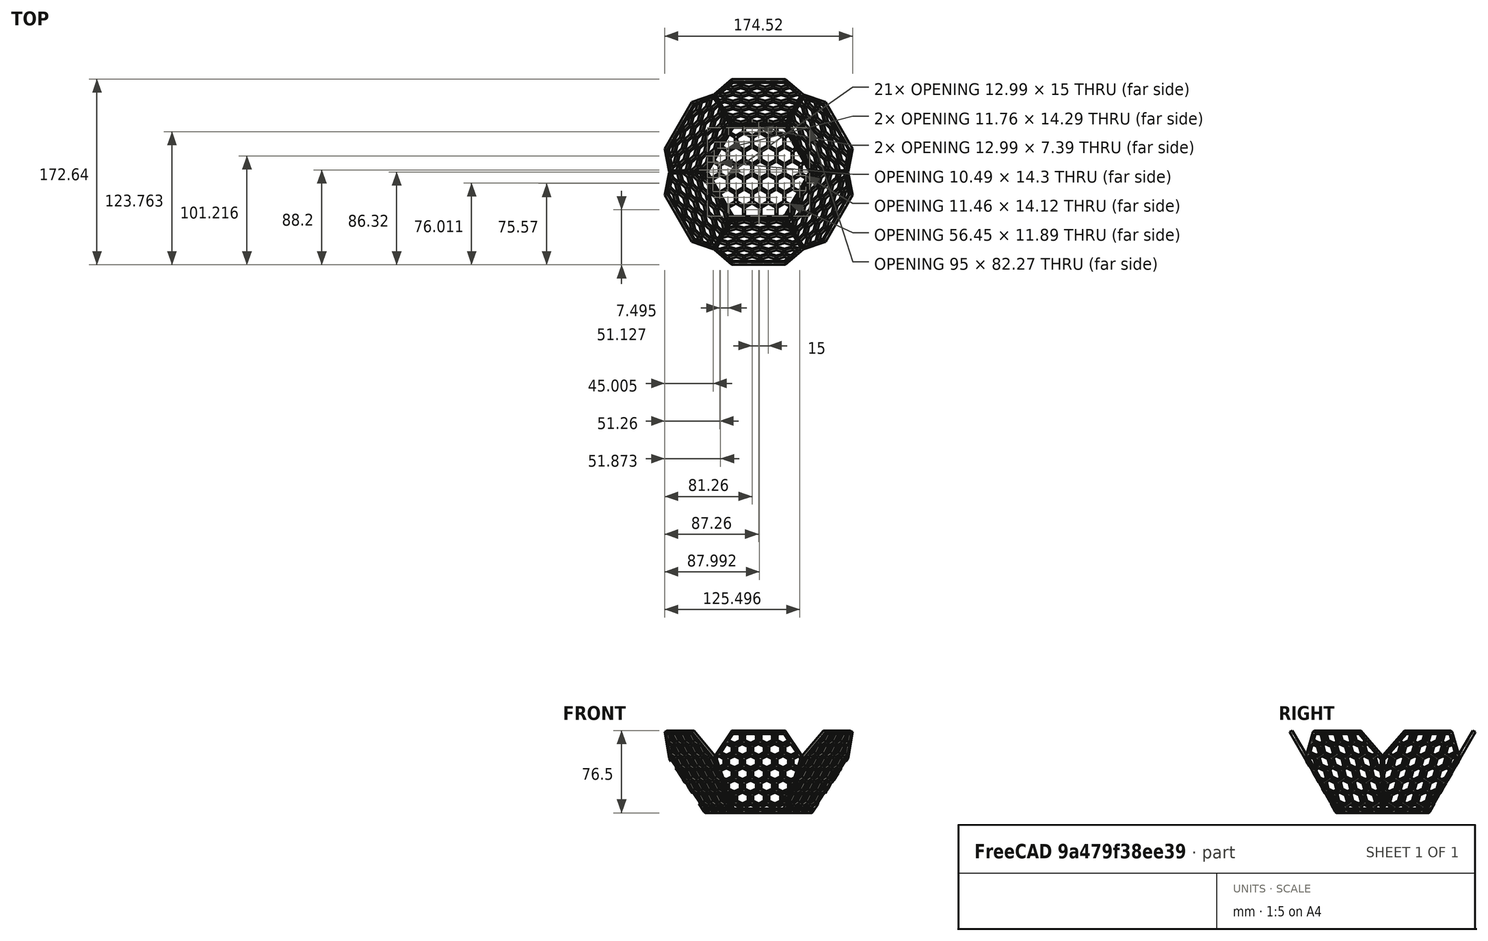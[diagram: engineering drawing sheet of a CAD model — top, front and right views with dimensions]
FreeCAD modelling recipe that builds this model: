
FCSTD DOCUMENT  (FreeCAD 0.20R29410 (Git))
Label: hexagon.v3
License: All rights reserved
LicenseURL: http://en.wikipedia.org/wiki/All_rights_reserved
objects: PartDesign::Body×8, Sketcher::SketchObject×6, Part::Cut×5, PartDesign::FeatureBase×4, Part::FeaturePython×3, Part::Extrusion×3, PartDesign::Pad×3, Part::Compound×2, Part::MultiFuse×2, Part::Mirroring×2, Part::Fuse×2, Spreadsheet::Sheet×1, Mesh::Feature×1
note: 42 computed .brp shape members not serialized (recipe doc carries the construction recipe); baked Part::Feature solids carry a one-line shape summary decoded from their .brp

FEATURE [Sketcher::SketchObject] Sketch  label="sHonycomb"
  FullyConstrained = true
  MapMode = 5
  Support = -> [XY_Plane]
  expr: .Constraints.HexR = <<Data>>.sHex_r
  expr: .Constraints.sHexD = <<Data>>.sHex_d
  sketch-geometry (18):
    g0: LineSegment StartX=0 StartY=11.25 StartZ=0 EndX=-6.49519 EndY=7.5 EndZ=0
    g1: LineSegment StartX=-6.49519 StartY=7.5 StartZ=0 EndX=-6.49519 EndY=9e-16 EndZ=0
    g2: LineSegment StartX=-6.49519 StartY=1e-15 StartZ=0 EndX=-9e-16 EndY=-3.75 EndZ=0
    g3: LineSegment StartX=-9e-16 StartY=-3.75 StartZ=0 EndX=6.49519 EndY=0 EndZ=0
    g4: LineSegment StartX=6.49519 StartY=0 StartZ=0 EndX=6.49519 EndY=7.5 EndZ=0
    g5: LineSegment StartX=6.49519 StartY=7.5 StartZ=0 EndX=0 EndY=11.25 EndZ=0
    g6: Circle CenterX=-1.1e-15 CenterY=3.75 CenterZ=0 NormalX=0 NormalY=0 NormalZ=1 AngleXU=0 Radius=7.5
    g7: LineSegment StartX=13.9904 StartY=-5.48205 StartZ=0 EndX=7.49519 EndY=-1.73205 EndZ=0
    g8: LineSegment StartX=7.49519 StartY=-1.73205 StartZ=0 EndX=1 EndY=-5.48205 EndZ=0
    g9: LineSegment StartX=1 StartY=-5.48205 StartZ=0 EndX=1 EndY=-12.9821 EndZ=0
    g10: LineSegment StartX=1 StartY=-12.9821 StartZ=0 EndX=7.49519 EndY=-16.7321 EndZ=0
    g11: LineSegment StartX=7.49519 StartY=-16.7321 StartZ=0 EndX=13.9904 EndY=-12.9821 EndZ=0
    g12: LineSegment StartX=13.9904 StartY=-12.9821 StartZ=0 EndX=13.9904 EndY=-5.48205 EndZ=0
    g13: Circle CenterX=7.49519 CenterY=-9.23205 CenterZ=0 NormalX=0 NormalY=0 NormalZ=1 AngleXU=0 Radius=7.5
    g14: LineSegment StartX=6.49519 StartY=0 StartZ=0 EndX=7.49519 EndY=-1.73205 EndZ=0
    g15: LineSegment StartX=7.49519 StartY=-1.73205 StartZ=0 EndX=8.49519 EndY=0 EndZ=0
    g16: LineSegment StartX=8.49519 StartY=0 StartZ=0 EndX=6.49519 EndY=0 EndZ=0
    g17: LineSegment StartX=6.49519 StartY=0 StartZ=0 EndX=-6.49519 EndY=1e-15 EndZ=0
  constraints (43):
    c: Coincident(g0,g1)
    c: Coincident(g1,g2)
    c: Coincident(g2,g3)
    c: Coincident(g3,g4)
    c: Coincident(g4,g5)
    c: Coincident(g5,g0)
    c: Equal(g0, g1-g5) x5
    c: PointOnObject(g0,g6)
    c: PointOnObject(g1,g6)
    c: PointOnObject(g2,g6)
    c: PointOnObject(g3,g6)
    c: PointOnObject(g4,g6)
    c: PointOnObject(g5,g6)
    c: Coincident(g7,g8)
    c: Coincident(g8,g9)
    c: Coincident(g9,g10)
    c: Coincident(g10,g11)
    c: Coincident(g11,g12)
    c: Coincident(g12,g7)
    c: Equal(g7, g8-g12) x5
    c: PointOnObject(g7,g13)
    c: PointOnObject(g8,g13)
    c: PointOnObject(g9,g13)
    c: PointOnObject(g10,g13)
    c: PointOnObject(g11,g13)
    c: PointOnObject(g12,g13)
    c: Equal(g6,g13)
    c: PointOnObject(g0,g-2)
    c: Vertical(g12)
    c: Radius(g6) = 7.5  'HexR'
    c: Vertical(g4)
    c: Coincident(g3,g14)
    c: Coincident(g14,g7)
    c: Coincident(g14,g15)
    c: PointOnObject(g15,g-1)
    c: Coincident(g15,g16)
    c: Coincident(g16,g14)
    c: Horizontal(g16)
    c: Equal(g15,g14)
    c: Equal(g14,g16)
    c: Distance(g16) = 2  'sHexD'
    c: Coincident(g17,g3)
    c: Coincident(g17,g1)
FEATURE [PartDesign::Body] Body  label="bHonycomSketch"
  Group = -> [Sketch]
  Origin = -> Origin
FEATURE [Part::FeaturePython] Array  label="ArrayofHonyComb"  # Draft array (typed FeaturePython)
  AlwaysSyncPlacement = false
  Angle = 360
  ArrayType = 0
  Axis = (0,0,1)
  Base = -> Sketch
  Center = (0,0,0)
  Count = 45
  ExpandArray = false
  Fuse = false
  IntervalAxis = (0,0,0)
  IntervalX = (15,0,0)
  IntervalY = (0,26,0)
  IntervalZ = (0,0,100)
  NumberCircles = 3
  NumberPolar = 5
  NumberX = 9
  NumberY = 5
  NumberZ = 1
  Placement = pos=(-81,-44,0) rot=(0,0,1;0rad)
  PlacementList = 45 placements: [(0,0,0),(0,26,0),(0,52,0),(0,78,0),(0,104,0),(15,0,0),(15,26,0),(15,52,0),(15,78,0),(15,104,0),(30,0,0),(30,26,0),(30,52,0),(30,78,0),(30,104,0),(45,0,0),(45,26,0),(45,52,0),(45,78,0),(45,104,0),(60,0,0),(60,26,0),(60,52,0),(60,78,0),(60,104,0),(75,0,0),(75,26,0),(75,52,0),(75,78,0),(75,104,0),(90,0,0),(90,26,0),(90,52,0),(90,78,0),(90,104,0),(105,0,0),(105,26,0),(105,52,0),(105,78,0),(105,104,0),+5 more]
  RadialDistance = 50
  ScaleList = (45) [(1,1,1),(1,1,1),(1,1,1),(1,1,1),(1,1,1),(1,1,1),(1,1,1),(1,1,1),(1,1,1),(1,1,1),(1,1,1),(1,1,1),(1,1,1),(1,1,1),(1,1,1),(1,1,1),(1,1,1),(1,1,1),+27 more]
  Symmetry = 1
  TangentialDistance = 25
FEATURE [Part::Extrusion] Extrude  label="HonyCombPart"
  Base = -> Array
  Dir = (0,0,1)
  DirMode = 2
  FaceMakerClass = Part::FaceMakerBullseye
  LengthFwd = 4
  LengthRev = 0
  Solid = true
  Symmetric = false
FEATURE [Sketcher::SketchObject] Sketch001  label="sHex"
  FullyConstrained = true
  MapMode = 5
  Support = -> [XY_Plane001]
  expr: Constraints[18] = <<Data>>.sFace_d - <<Data>>.sRing_w
  expr: Constraints[39] = <<Data>>.sFace_d
  sketch-geometry (14):
    g0: LineSegment StartX=23.75 StartY=41.1362 StartZ=0 EndX=-23.75 EndY=41.1362 EndZ=0
    g1: LineSegment StartX=-23.75 StartY=41.1362 StartZ=0 EndX=-47.5 EndY=8.53e-14 EndZ=0
    g2: LineSegment StartX=-47.5 StartY=8.71e-14 StartZ=0 EndX=-23.75 EndY=-41.1362 EndZ=0
    g3: LineSegment StartX=-23.75 StartY=-41.1362 StartZ=0 EndX=23.75 EndY=-41.1362 EndZ=0
    g4: LineSegment StartX=23.75 StartY=-41.1362 StartZ=0 EndX=47.5 EndY=7.82e-14 EndZ=0
    g5: LineSegment StartX=47.5 StartY=7.83e-14 StartZ=0 EndX=23.75 EndY=41.1362 EndZ=0
    g6: Circle CenterX=0 CenterY=0 CenterZ=0 NormalX=0 NormalY=0 NormalZ=1 AngleXU=0 Radius=47.5
    g7: LineSegment StartX=-25 StartY=43.3013 StartZ=0 EndX=-50 EndY=0 EndZ=0
    g8: LineSegment StartX=-50 StartY=-8e-16 StartZ=0 EndX=-25 EndY=-43.3013 EndZ=0
    g9: LineSegment StartX=-25 StartY=-43.3013 StartZ=0 EndX=25 EndY=-43.3013 EndZ=0
    g10: LineSegment StartX=25 StartY=-43.3013 StartZ=0 EndX=50 EndY=7.1e-15 EndZ=0
    g11: LineSegment StartX=50 StartY=3.8e-15 StartZ=0 EndX=25 EndY=43.3013 EndZ=0
    g12: LineSegment StartX=25 StartY=43.3013 StartZ=0 EndX=-25 EndY=43.3013 EndZ=0
    g13: Circle CenterX=0 CenterY=0 CenterZ=0 NormalX=0 NormalY=0 NormalZ=1 AngleXU=0 Radius=50
  constraints (32):
    c: Coincident(g0,g1)
    c: Coincident(g1,g2)
    c: Coincident(g2,g3)
    c: Coincident(g3,g4)
    c: Coincident(g4,g5)
    c: Coincident(g5,g0)
    c: Equal(g0, g1-g5) x5
    c: PointOnObject(g0,g6)
    c: PointOnObject(g1,g6)
    c: PointOnObject(g2,g6)
    c: PointOnObject(g3,g6)
    c: PointOnObject(g4,g6)
    c: PointOnObject(g5,g6)
    c: Coincident(g6,g-1)
    c: Diameter(g6) = 95
    c: Horizontal(g0)
    c: Coincident(g7,g8)
    c: Coincident(g8,g9)
    c: Coincident(g9,g10)
    c: Coincident(g10,g11)
    c: Coincident(g11,g12)
    c: Coincident(g12,g7)
    c: Equal(g7, g8-g12) x5
    c: PointOnObject(g7,g13)
    c: PointOnObject(g8,g13)
    c: PointOnObject(g9,g13)
    c: PointOnObject(g10,g13)
    c: PointOnObject(g11,g13)
    c: PointOnObject(g12,g13)
    c: Coincident(g13,g6)
    c: Parallel(g12,g0)
    c: Diameter(g13) = 100
FEATURE [PartDesign::Pad] Pad  label="pHexShapeRing"
  Direction = (0,0,1)
  Length = 3
  Length2 = 10
  Profile = -> Sketch001
  ReferenceAxis = -> Sketch001 [N_Axis]
  Refine = true
  Type = 0
FEATURE [PartDesign::Body] Body001  label="bHexShapeRing"
  Group = -> [Sketch001,Pad]
  Origin = -> Origin001
  Tip = -> Pad
FEATURE [Part::Compound] Compound  label="ring"
  Links = -> [Pad]
FEATURE [Sketcher::SketchObject] Sketch002
  FullyConstrained = true
  MapMode = 5
  Support = -> [XY_Plane002]
  expr: Constraints[18] = <<Data>>.sFace_d - <<Data>>.sRing_w + 2
  sketch-geometry (7):
    g0: LineSegment StartX=24.25 StartY=42.0022 StartZ=0 EndX=-24.25 EndY=42.0022 EndZ=0
    g1: LineSegment StartX=-24.25 StartY=42.0022 StartZ=0 EndX=-48.5 EndY=8.53e-14 EndZ=0
    g2: LineSegment StartX=-48.5 StartY=8.61e-14 StartZ=0 EndX=-24.25 EndY=-42.0022 EndZ=0
    g3: LineSegment StartX=-24.25 StartY=-42.0022 StartZ=0 EndX=24.25 EndY=-42.0022 EndZ=0
    g4: LineSegment StartX=24.25 StartY=-42.0022 StartZ=0 EndX=48.5 EndY=8.53e-14 EndZ=0
    g5: LineSegment StartX=48.5 StartY=8.61e-14 StartZ=0 EndX=24.25 EndY=42.0022 EndZ=0
    g6: Circle CenterX=0 CenterY=0 CenterZ=0 NormalX=0 NormalY=0 NormalZ=1 AngleXU=0 Radius=48.5
  constraints (16):
    c: Coincident(g0,g1)
    c: Coincident(g1,g2)
    c: Coincident(g2,g3)
    c: Coincident(g3,g4)
    c: Coincident(g4,g5)
    c: Coincident(g5,g0)
    c: Equal(g0, g1-g5) x5
    c: PointOnObject(g0,g6)
    c: PointOnObject(g1,g6)
    c: PointOnObject(g2,g6)
    c: PointOnObject(g3,g6)
    c: PointOnObject(g4,g6)
    c: PointOnObject(g5,g6)
    c: Coincident(g6,g-1)
    c: Diameter(g6) = 97
    c: Horizontal(g0)
FEATURE [PartDesign::Pad] Pad001
  Direction = (0,0,1)
  Length = 3
  Length2 = 10
  Profile = -> Sketch002
  ReferenceAxis = -> Sketch002 [N_Axis]
  Refine = true
  Type = 0
FEATURE [PartDesign::Body] Body002  label="solidHexBody"
  Group = -> [Sketch002,Pad001]
  Origin = -> Origin002
  Tip = -> Pad001
FEATURE [Part::Compound] Compound001
  Links = -> [Body002]
FEATURE [Part::Cut] Cut  label="HwxHonycomb"
  Base = -> Compound001
  Placement = pos=(0,-1,0) rot=(0,0,1;0rad)
  Refine = true
  Tool = -> Extrude
FEATURE [Part::MultiFuse] Fusion  label="basicShape"
  Refine = true
  Shapes = -> [Compound,Cut]
FEATURE [Sketcher::SketchObject] Sketch003  label="sTriimEdge"
  FullyConstrained = true
  MapMode = 5
  Placement = pos=(0,0,0) rot=(0.57735,0.57735,0.57735;2.0944rad)
  Support = -> [YZ_Plane004]
  sketch-geometry (3):
    g0: LineSegment StartX=4.046e-13 StartY=5.19615 StartZ=0 EndX=-3 EndY=0 EndZ=0
    g1: LineSegment StartX=-3 StartY=0 StartZ=0 EndX=3 EndY=0 EndZ=0
    g2: LineSegment StartX=3 StartY=0 StartZ=0 EndX=4.046e-13 EndY=5.19615 EndZ=0
  constraints (8):
    c: Coincident(g0,g1)
    c: Horizontal(g1)
    c: Coincident(g1,g2)
    c: Coincident(g2,g0)
    c: Equal(g2,g0)
    c: Equal(g0,g1)
    c: Symmetric(g1,g0,g-1)
    c: Distance(g2) = 6
FEATURE [PartDesign::Pad] Pad002  label="pTrimEdge"
  Direction = (1,-2e-16,3e-16)
  Length = 100
  Length2 = 10
  Midplane = true
  Placement = pos=(0,0,0) rot=(0.57735,0.57735,0.57735;2.0944rad)
  Profile = -> Sketch003
  ReferenceAxis = -> Sketch003 [N_Axis]
  Refine = true
  Type = 0
  expr: Length = 100
FEATURE [PartDesign::Body] Body004  label="bTrimEdge"
  Group = -> [Sketch003,Pad002]
  Origin = -> Origin004
  Placement = pos=(0,-7,-6) rot=(0,0,1;0rad)
  Tip = -> Pad002
FEATURE [Spreadsheet::Sheet] Spreadsheet  label="Data"
  cells = A3=sHex-r; B3(sHex_r)=7.5; D3=Honycom cell size; A4=sHex-d; B4(sHex_d)=2; D4=HonyComp distance between cells; A5=sFace_d; B5(sFace_d)=100; A6=sRing_w; B6(sRing_w)=5
FEATURE [PartDesign::FeatureBase] Clone
  BaseFeature = -> Fusion
FEATURE [PartDesign::Body] Body017  label="Baset1"
  BaseFeature = -> Fusion
  Group = -> [Clone]
  Origin = -> Origin017
  Tip = -> Clone
FEATURE [PartDesign::FeatureBase] Clone001
  BaseFeature = -> Body004
  Placement = pos=(0,2,-6) rot=(0,0,1;0rad)
FEATURE [PartDesign::Body] Body018  label="bTrimedget1"
  BaseFeature = -> Body004
  Group = -> [Clone001]
  Origin = -> Origin018
  Placement = pos=(0,-47,5) rot=(0,0,1;0rad)
  Tip = -> Clone001
FEATURE [Part::FeaturePython] Array001  # Draft array (typed FeaturePython)
  AlwaysSyncPlacement = false
  Angle = 360
  ArrayType = 1
  Axis = (0,0,1)
  Base = -> Body018
  Center = (0,0,0)
  Count = 6
  ExpandArray = false
  Fuse = true
  IntervalAxis = (0,0,0)
  IntervalX = (50,0,0)
  IntervalY = (0,50,0)
  IntervalZ = (0,0,50)
  NumberCircles = 3
  NumberPolar = 6
  NumberX = 2
  NumberY = 2
  NumberZ = 1
  PlacementList = 6 placements: [(0,-47,5),(40.7032,-23.5,5),(40.7032,23.5,5),(5.75584e-15,47,5),(-40.7032,23.5,5),(-40.7032,-23.5,5)]
  RadialDistance = 50
  ScaleList = (6) [(1,1,1),(1,1,1),(1,1,1),(1,1,1),(1,1,1),(1,1,1)]
  Symmetry = 1
  TangentialDistance = 25
FEATURE [Part::Cut] Cut001  label="base"
  Base = -> Body017
  Placement = pos=(0,0,3) rot=(1,0,0;3.14159rad)
  Refine = true
  Tool = -> Array001
FEATURE [PartDesign::FeatureBase] Clone002
  BaseFeature = -> Fusion
FEATURE [PartDesign::Body] Body019  label="facetemp1"
  BaseFeature = -> Fusion
  Group = -> [Clone002]
  Origin = -> Origin019
  Tip = -> Clone002
FEATURE [PartDesign::FeatureBase] Clone003
  BaseFeature = -> Body004
  Placement = pos=(-4,-44,-1) rot=(0,0,1;0rad)
FEATURE [PartDesign::Body] Body020
  BaseFeature = -> Body004
  Group = -> [Clone003]
  Origin = -> Origin020
  Tip = -> Clone003
FEATURE [Part::Cut] Cut002  label="facetempEdgeTrimed"
  Base = -> Body019
  Refine = true
  Tool = -> Body020
FEATURE [Sketcher::SketchObject] Sketch004
  FullyConstrained = false
  MapMode = 2
  Support = -> [Cut002]
  sketch-geometry (3):
    g0: LineSegment StartX=-25.3699 StartY=-43.3886 StartZ=0 EndX=-50.761 EndY=0.597581 EndZ=0
    g1: LineSegment StartX=-50.761 StartY=0.597581 StartZ=0 EndX=-41.6902 EndY=16.3061 EndZ=0
    g2: LineSegment StartX=-41.6902 StartY=16.3061 StartZ=0 EndX=-25.3699 EndY=-43.3886 EndZ=0
  constraints (4):
    c: Coincident(g1,g0)
    c: Angle(g0,g1) = 2.0944
    c: Coincident(g2,g1)
    c: Coincident(g2,g0)
FEATURE [Part::Extrusion] Extrude001  label="adjustFaceCut"
  Base = -> Sketch004
  Dir = (0,0,1)
  DirMode = 2
  FaceMakerClass = Part::FaceMakerBullseye
  LengthFwd = 10
  LengthRev = 0
  Solid = true
  Symmetric = true
FEATURE [Part::Mirroring] Part__Mirroring  label="adjustFaceCut (Mirror #1)"
  Base = (0,0,0)
  Normal = (1,0,0)
  Source = -> Extrude001
FEATURE [Part::Cut] Cut003  label="facetempLeftCut"
  Base = -> Cut002
  Refine = true
  Tool = -> Extrude001
FEATURE [Part::Cut] Cut004  label="facetempLeftRightCut"
  Base = -> Cut003
  Refine = true
  Tool = -> Part__Mirroring
FEATURE [Sketcher::SketchObject] Sketch005
  ExternalGeometry = -> [Cut004]
  FullyConstrained = true
  MapMode = 2
  sketch-geometry (4):
    g0: LineSegment StartX=-41.3353 StartY=15.0078 StartZ=0 EndX=-25 EndY=-43.3013 EndZ=0
    g1: LineSegment StartX=-25 StartY=-43.3013 StartZ=0 EndX=-23 EndY=-43.3013 EndZ=0
    g2: LineSegment StartX=-23 StartY=-43.3013 StartZ=0 EndX=-39.9887 EndY=17.3401 EndZ=0
    g3: LineSegment StartX=-39.9887 StartY=17.3401 StartZ=0 EndX=-41.3353 EndY=15.0078 EndZ=0
  constraints (10):
    c: Coincident(g-4,g0)
    c: Coincident(g0,g-5)
    c: Coincident(g0,g1)
    c: PointOnObject(g1,g-5)
    c: Coincident(g1,g2)
    c: PointOnObject(g2,g-4)
    c: Coincident(g2,g3)
    c: Coincident(g3,g0)
    c: Distance(g1) = 2
    c: Parallel(g2,g0)
FEATURE [Part::Extrusion] Extrude002
  Base = -> Sketch005
  Dir = (0,0,1)
  DirMode = 2
  FaceMakerClass = Part::FaceMakerBullseye
  LengthFwd = 2
  LengthRev = 0
  Solid = true
  Symmetric = false
FEATURE [Part::Mirroring] Part__Mirroring001  label="Extrude002 (Mirror #2)"
  Base = (0,0,0)
  Normal = (1,0,0)
  Source = -> Extrude002
FEATURE [Part::Fuse] Fusion001
  Base = -> Cut004
  Refine = true
  Tool = -> Extrude002
FEATURE [Part::Fuse] Fusion002  label="finalFaceinPlace"
  Base = -> Part__Mirroring001
  Placement = pos=(0,-62.0718,38.1436) rot=(1,0,0;2.0944rad)
  Refine = true
  Tool = -> Fusion001
FEATURE [Part::FeaturePython] Array002  label="facesInPlace"  # Draft array (typed FeaturePython)
  AlwaysSyncPlacement = false
  Angle = 360
  ArrayType = 1
  Axis = (0,0,1)
  Base = -> Fusion002
  Center = (0,0,0)
  Count = 6
  ExpandArray = false
  Fuse = true
  IntervalAxis = (0,0,0)
  IntervalX = (50,0,0)
  IntervalY = (0,50,0)
  IntervalZ = (0,0,50)
  NumberCircles = 3
  NumberPolar = 6
  NumberX = 2
  NumberY = 2
  NumberZ = 1
  PlacementList = 6 placements: [(0,-62.0718,38.1436),(53.7558,-31.0359,38.1436),(53.7558,31.0359,38.1436),(7.6016e-15,62.0718,38.1436),(-53.7558,31.0359,38.1436),(-53.7558,-31.0359,38.1436)]
  RadialDistance = 50
  ScaleList = (6) [(1,1,1),(1,1,1),(1,1,1),(1,1,1),(1,1,1),(1,1,1)]
  Symmetry = 1
  TangentialDistance = 25
FEATURE [Part::MultiFuse] Fusion003  label="bowl"
  Refine = true
  Shapes = -> [Cut001,Array002]
FEATURE [Mesh::Feature] Mesh  label="bowl (Meshed)"
